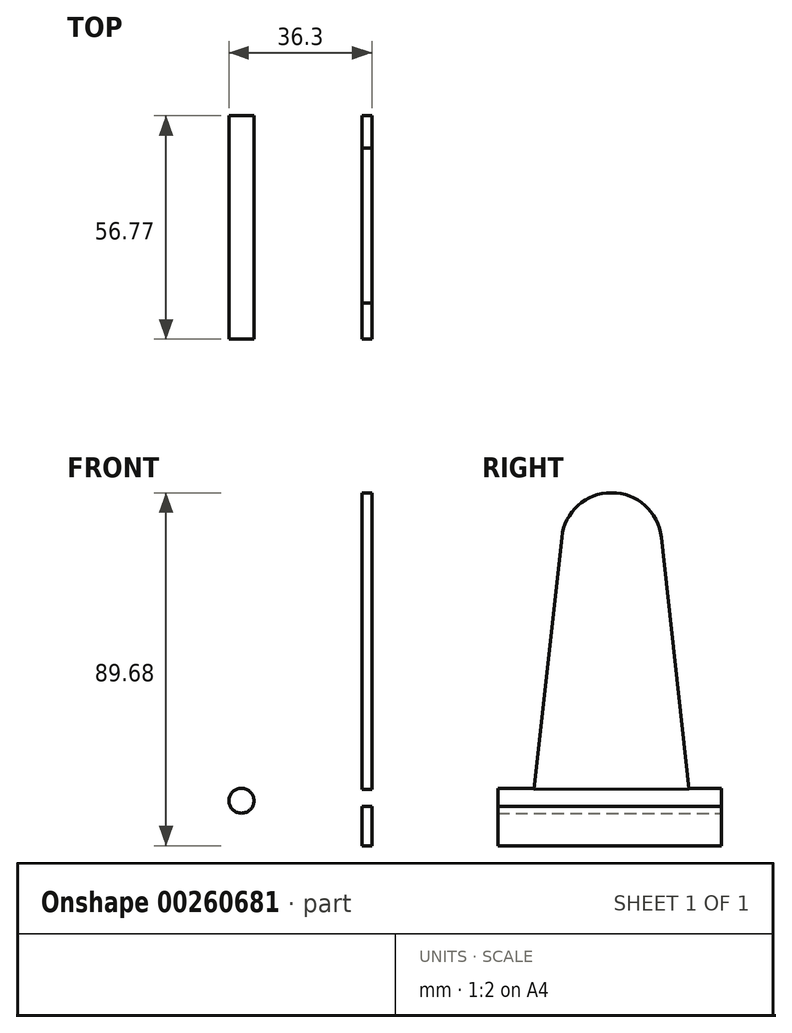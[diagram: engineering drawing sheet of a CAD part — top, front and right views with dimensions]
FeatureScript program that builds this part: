
annotation { "Feature Type Name" : "Feature", "Feature Type Description" : "" }
export const myFeature = defineFeature(function(context is Context, id is Id, definition is map)
    precondition{}
    {
        {
            var Q0;
            Q0=qCreatedBy(makeId("Front.planeOp"),FACE);
            var sketch = newSketch(context, id + "F0", { "sketchPlane" : qUnion([Q0])});
            skCircle(sketch, "E0", {"center": v(-30.59, 27.93) * mm, "radius": 3.18 * mm});
            skSolve(sketch);
        }
        {
            var Q0;
            Q0 = qSketchRegion(id + "F0", true);
            extrude(context, id + "F1", {"entities" : qUnion([Q0]), "depth" : 56.77 * mm});
        }
        {
            var Q0;
            Q0=qCreatedBy(makeId("Right.planeOp"),FACE);
            var sketch = newSketch(context, id + "F2", { "sketchPlane" : qUnion([Q0])});
            skLineSegment(sketch, "E1", {"start": v(0, 26.52) * mm, "end": v(-56.77, 26.52) * mm});
            skLineSegment(sketch, "E2", {"start": v(-56.77, 26.52) * mm, "end": v(-56.77, 16.5) * mm});
            skLineSegment(sketch, "E3", {"start": v(-56.77, 16.5) * mm, "end": v(0, 16.5) * mm});
            skLineSegment(sketch, "E4", {"start": v(0, 16.5) * mm, "end": v(0, 26.52) * mm});
            skSolve(sketch);
        }
        {
            var Q0;
            {var subQ0=sQuery(id+"F2.wireOp",EDGE,"XnlaJZ7z-YqnE-tKj1-212I-39YF1K0jriu3");Q0=makeQuery(id+"F2.imprint","IMPRINT",FACE,{"disambiguationData":[TD([[makeQuery(id+"F2.imprint","IMPRINT",EDGE,{"derivedFrom":subQ0}),1.0]])]});}
            var Q1;
            {var subQ0=sQuery(id+"F2.wireOp",EDGE,"E1IniJ7O-zyJP-08zy-IwuA-LoQDIoecyXl4");var subQ1=sQuery(id+"F2.wireOp",EDGE,"uSvgNCe8-WuJh-WXKS-NHD4-OmyVd4OFrAlH");var subQ2=makeQuery(id+"F2.imprint","INTERSECT",VERTEX,{"disambiguationData":[OD(0.0)],"derivedFrom":[subQ1,subQ0]});Q1=makeQuery(id+"F2.imprint","IMPRINT",FACE,{"disambiguationData":[TD([[makeQuery(id+"F2.imprint","IMPRINT",EDGE,{"disambiguationData":[TD([[subQ2,1.0]])],"derivedFrom":subQ1}),1.0]])]});}
            var Q2;
            Q2=makeQuery(id+"F2.imprint","IMPRINT",FACE,{"disambiguationData":[TD([[makeQuery(id+"F2.imprint","IMPRINT",EDGE,{"derivedFrom":sQuery(id+"F2.wireOp",EDGE,"E1")}),1.0]])]});
            extrude(context, id + "F3", {"entities" : qUnion([Q0, Q1, Q2]), "depth" : 2.54 * mm});
        }
        {
            var Q0;
            Q0=qCreatedBy(makeId("Right.planeOp"),FACE);
            var sketch = newSketch(context, id + "F4", { "sketchPlane" : qUnion([Q0])});
            skCircle(sketch, "E5", {"center": v(-27.88, 93.46) * mm, "radius": 12.72 * mm});
            skLineSegment(sketch, "E6", {"start": v(-15.23, 94.86) * mm, "end": v(-8.15, 31) * mm});
            skLineSegment(sketch, "E7", {"start": v(-40.52, 94.84) * mm, "end": v(-47.53, 30.76) * mm});
            skLineSegment(sketch, "E8", {"start": v(-47.53, 30.76) * mm, "end": v(-8.15, 31) * mm});
            skSolve(sketch);
        }
        {
            var Q0;
            {var subQ0=sQuery(id+"F4.wireOp",EDGE,"E6");Q0=makeQuery(id+"F4.imprint","IMPRINT",FACE,{"disambiguationData":[TD([[makeQuery(id+"F4.imprint","IMPRINT",EDGE,{"derivedFrom":subQ0}),-1.0]])]});}
            var Q1;
            {var subQ0=sQuery(id+"F4.wireOp",EDGE,"E5");var subQ1=makeQuery(id+"F4.imprint","INTERSECT",VERTEX,{"derivedFrom":[subQ0,sQuery(id+"F4.wireOp",EDGE,"E6")]});Q1=makeQuery(id+"F4.imprint","IMPRINT",FACE,{"disambiguationData":[TD([[makeQuery(id+"F4.imprint","IMPRINT",EDGE,{"disambiguationData":[TD([[subQ1,-1.0]])],"derivedFrom":subQ0}),1.0]])]});}
            extrude(context, id + "F5", {"entities" : qUnion([Q0, Q1]), "depth" : 2.54 * mm});
        }
    });
